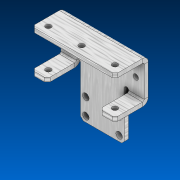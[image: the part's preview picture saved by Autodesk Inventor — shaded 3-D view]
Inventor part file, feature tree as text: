
AUTODESK INVENTOR PART (.ipt)
format: ipt  version: 2022.2 (Build 262287000, 287)  size: 165,376 bytes
history: native  units: in
note: dims shown in document units (in); Inventor stores cm internally (conversion verified against a paired STEP export)
features: chamfer x1
ambient origin geometry x8: Origin, YZ Plane, XZ Plane, XY Plane, X Axis, Y Axis, Z Axis, Center Point
bodies: Solid1 (feature_tree)
feature tree (1):
  chamfer  "Chamfer1"  [1 undecoded]
note: 1 required parameter value undecoded (feature->parameter linkage not recoverable at this tier; creation-order binding heuristic only, values carry confidence <= 0.55)
